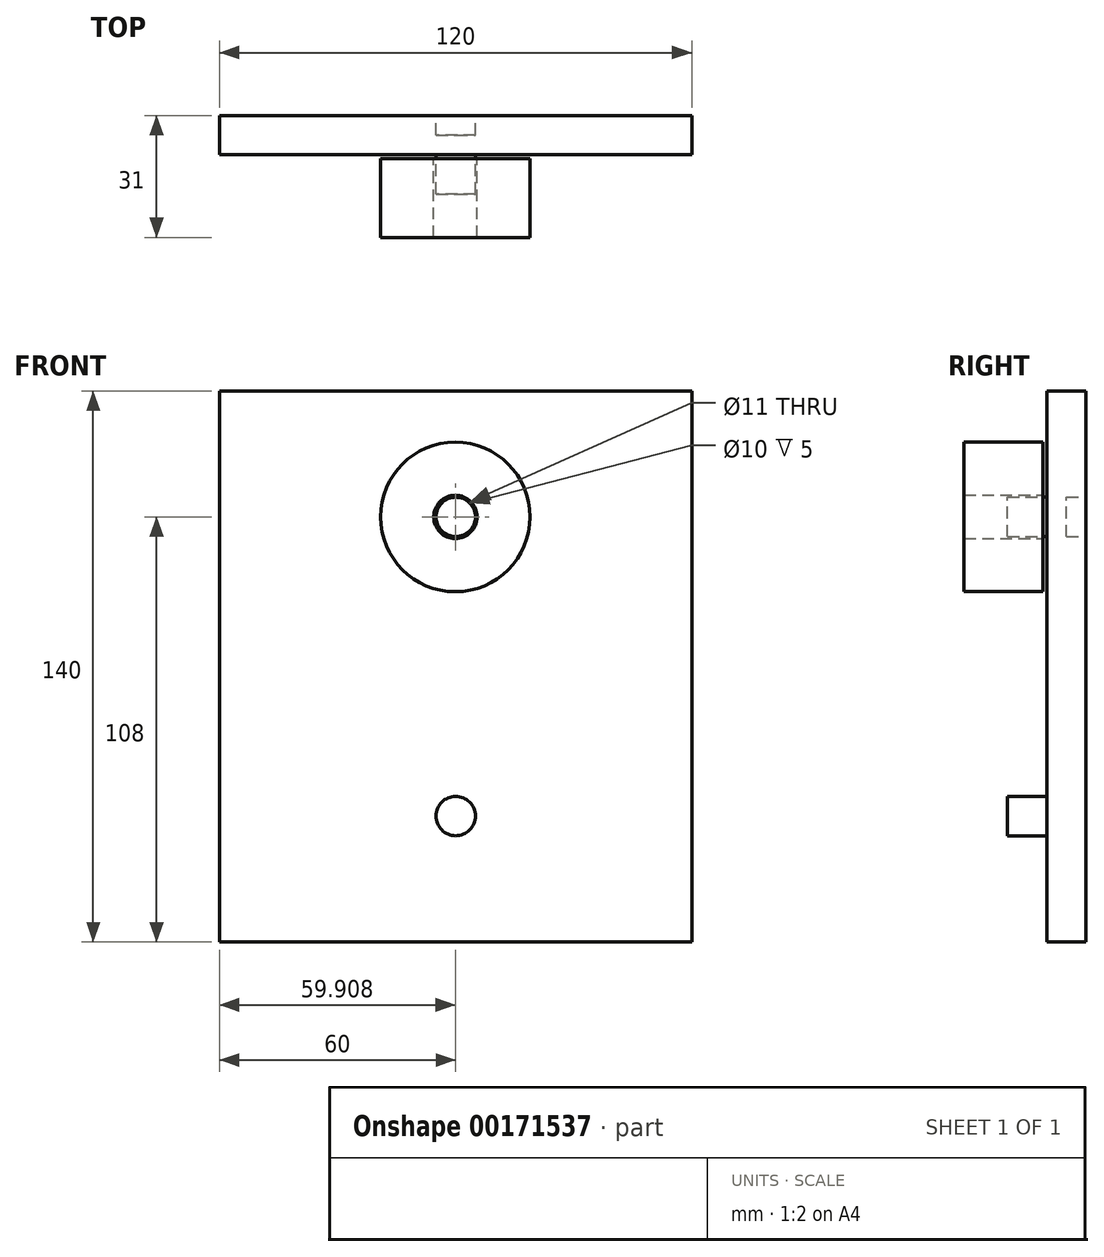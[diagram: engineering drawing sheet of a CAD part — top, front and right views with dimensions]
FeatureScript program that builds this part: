
annotation { "Feature Type Name" : "Feature", "Feature Type Description" : "" }
export const myFeature = defineFeature(function(context is Context, id is Id, definition is map)
    precondition{}
    {
        {
            var Q0;
            Q0=qCreatedBy(makeId("Front.planeOp"),FACE);
            var sketch = newSketch(context, id + "F0", { "sketchPlane" : qUnion([Q0])});
            skLineSegment(sketch, "E0.bottom", {"start": v(60, 70) * mm, "end": v(-60, 70) * mm});
            skLineSegment(sketch, "E0.top", {"start": v(60, -70) * mm, "end": v(-60, -70) * mm});
            skLineSegment(sketch, "E0.left", {"start": v(60, 70) * mm, "end": v(60, -70) * mm});
            skLineSegment(sketch, "E0.right", {"start": v(-60, 70) * mm, "end": v(-60, -70) * mm});
            skPoint(sketch, "E0.middle", {"position": v(0, 0) * mm});
            skLineSegment(sketch, "E1.bottom", {"start": v(60, 19) * mm, "end": v(-60, 19) * mm, "construction": true});
            skLineSegment(sketch, "E1.top", {"start": v(60, -19) * mm, "end": v(-60, -19) * mm, "construction": true});
            skLineSegment(sketch, "E1.left", {"start": v(60, 19) * mm, "end": v(60, -19) * mm, "construction": true});
            skLineSegment(sketch, "E1.right", {"start": v(-60, 17.79) * mm, "end": v(-60, -19) * mm, "construction": true});
            skCircle(sketch, "E2", {"center": v(0, 38) * mm, "radius": 5 * mm});
            skCircle(sketch, "E3", {"center": v(0, -38) * mm, "radius": 5 * mm, "construction": true});
            skCircle(sketch, "E4", {"center": v(0, 38) * mm, "radius": 19 * mm, "construction": true});
            skSolve(sketch);
        }
        {
            var Q0;
            Q0 = qSketchRegion(id + "F0", true);
            var Q1;
            Q1=makeQuery(id+"F0.imprint","IMPRINT",FACE,{"disambiguationData":[TD([[makeQuery(id+"F0.imprint","IMPRINT",EDGE,{"derivedFrom":sQuery(id+"F0.wireOp",EDGE,"E2")}),1.0]])]});
            extrude(context, id + "F1", {"entities" : qUnion([Q0, Q1]), "depth" : 10 * mm});
        }
        {
            var Q0;
            Q0=makeQuery(id+"F0.imprint","IMPRINT",FACE,{"disambiguationData":[TD([[makeQuery(id+"F0.imprint","IMPRINT",EDGE,{"derivedFrom":sQuery(id+"F0.wireOp",EDGE,"E2")}),1.0]])]});
            extrude(context, id + "F2", {"entities" : qUnion([Q0]), "operationType" : NewBodyOperationType.REMOVE, "depth" : 5 * mm});
        }
        {
            var Q0;
            Q0=makeQuery(id+"F1.opExtrude","CAP_FACE",FACE,{"disambiguationData":[OSD([sQuery(id+"F0.wireOp",EDGE,"E0.bottom"),sQuery(id+"F0.wireOp",EDGE,"E0.top"),sQuery(id+"F0.wireOp",EDGE,"E0.left"),sQuery(id+"F0.wireOp",EDGE,"E0.right")])],"isStart":false});
            var sketch = newSketch(context, id + "F3", { "sketchPlane" : qUnion([Q0])});
            skCircle(sketch, "E5", {"center": v(0, 38) * mm, "radius": 5 * mm});
            skPoint(sketch, "E6", {"position": v(0, 19) * mm});
            skCircle(sketch, "E7.MirrorC", {"center": v(0, -38) * mm, "radius": 5 * mm});
            skSolve(sketch);
        }
        {
            var Q0;
            Q0 = qSketchRegion(id + "F3", true);
            extrude(context, id + "F4", {"entities" : qUnion([Q0]), "operationType" : NewBodyOperationType.ADD, "depth" : 10 * mm});
        }
        {
            var Q0;
            Q0=makeQuery(id+"F1.opExtrude","CAP_FACE",FACE,{"disambiguationData":[OSD([sQuery(id+"F0.wireOp",EDGE,"E0.bottom"),sQuery(id+"F0.wireOp",EDGE,"E0.top"),sQuery(id+"F0.wireOp",EDGE,"E0.left"),sQuery(id+"F0.wireOp",EDGE,"E0.right")])],"isStart":false});
            cPlane(context, id + "F5", {"entities" : qUnion([Q0]), "cplaneType" : CPlaneType.OFFSET, "offset" : 1 * mm, "width" : 150 * mm, "height" : 150 * mm});
        }
        {
            var Q0;
            Q0=qCreatedBy(id+"F5.planeOp",FACE);
            var sketch = newSketch(context, id + "F6", { "sketchPlane" : qUnion([Q0])});
            skCircle(sketch, "E8", {"center": v(-0.1, 38) * mm, "radius": 19 * mm});
            skCircle(sketch, "E9", {"center": v(-0.1, 38) * mm, "radius": 5.5 * mm});
            skSolve(sketch);
        }
        {
            var Q0;
            Q0 = qSketchRegion(id + "F6", true);
            extrude(context, id + "F7", {"entities" : qUnion([Q0]), "depth" : 20 * mm});
        }
    });
